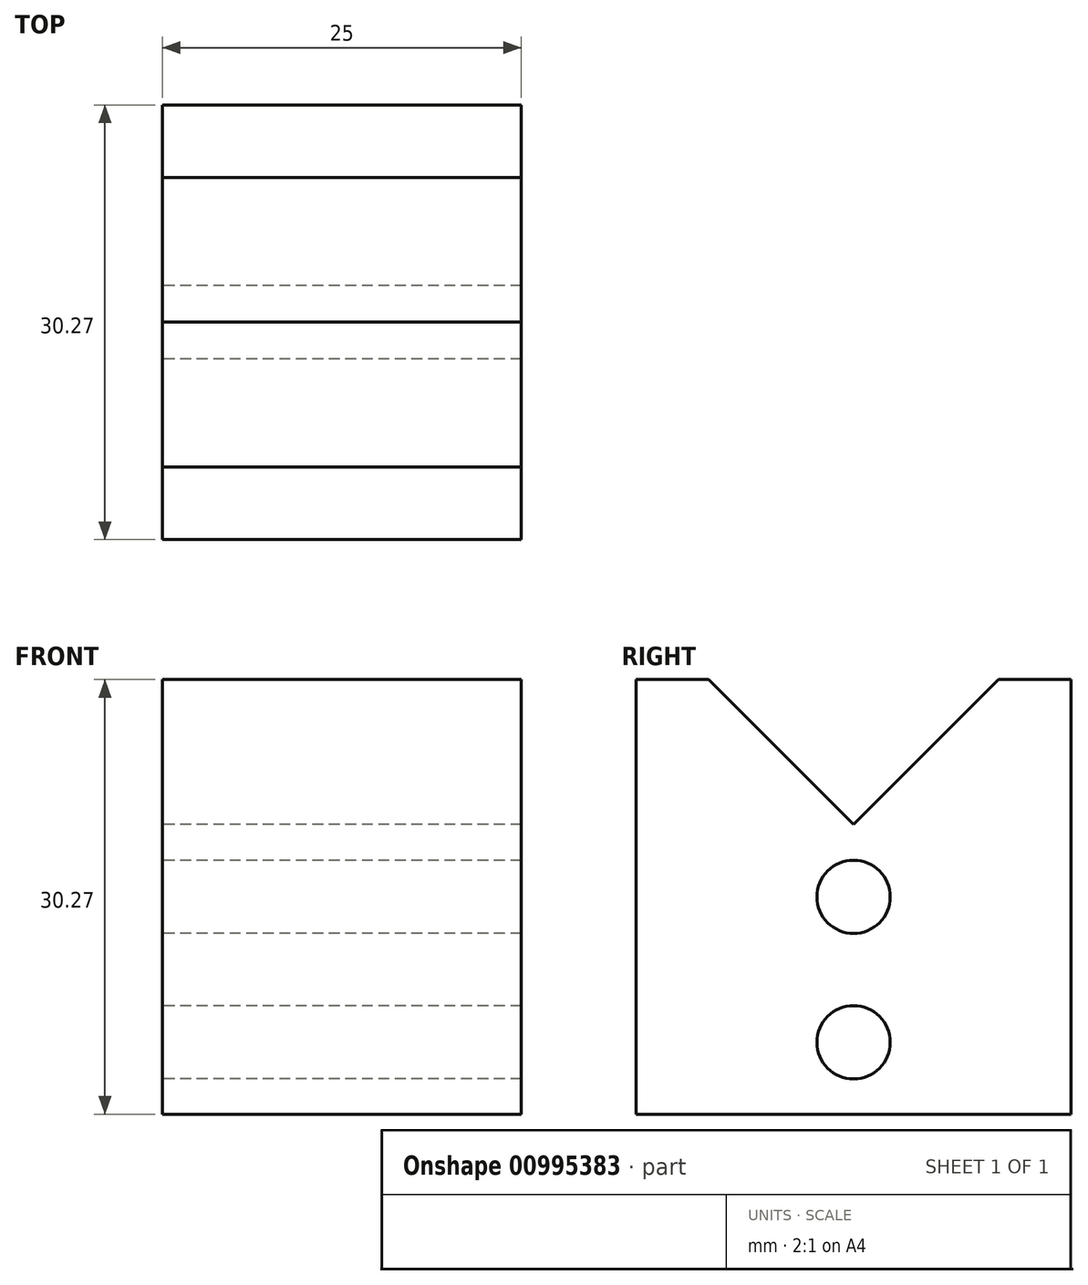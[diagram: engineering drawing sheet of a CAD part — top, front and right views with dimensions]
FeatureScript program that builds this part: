
annotation { "Feature Type Name" : "Feature", "Feature Type Description" : "" }
export const myFeature = defineFeature(function(context is Context, id is Id, definition is map)
    precondition{}
    {
        {
            var Q0;
            Q0=qCreatedBy(makeId("Right.planeOp"),FACE);
            var sketch = newSketch(context, id + "F0", { "sketchPlane" : qUnion([Q0])});
            skLineSegment(sketch, "E0.top", {"start": v(19.07, 30.27) * mm, "end": v(49.34, 30.27) * mm});
            skLineSegment(sketch, "E0.left", {"start": v(19.07, 0) * mm, "end": v(19.07, 30.27) * mm});
            skLineSegment(sketch, "E0.right", {"start": v(49.34, 0) * mm, "end": v(49.34, 30.27) * mm});
            skLineSegment(sketch, "E1", {"start": v(34.2, 20.18) * mm, "end": v(44.3, 30.27) * mm});
            skLineSegment(sketch, "E2", {"start": v(34.2, 20.18) * mm, "end": v(24.12, 30.27) * mm});
            skLineSegment(sketch, "E3", {"start": v(34.2, 30.27) * mm, "end": v(44.3, 30.27) * mm, "construction": true});
            skLineSegment(sketch, "E4", {"start": v(19.07, 0) * mm, "end": v(49.34, 0) * mm});
            skLineSegment(sketch, "E5", {"start": v(34.2, 20.18) * mm, "end": v(34.2, 0) * mm, "construction": true});
            skLineSegment(sketch, "E6", {"start": v(49.34, 30.27) * mm, "end": v(19.07, 0) * mm, "construction": true});
            skLineSegment(sketch, "E7", {"start": v(19.07, 30.27) * mm, "end": v(49.34, 0) * mm, "construction": true});
            skPoint(sketch, "E8", {"position": v(34.2, 15.14) * mm});
            skPoint(sketch, "E9", {"position": v(34.2, 10.1) * mm});
            skPoint(sketch, "E10", {"position": v(34.2, 5) * mm});
            skSolve(sketch);
        }
        {
            var Q0;
            Q0=makeQuery(id+"F0.imprint","IMPRINT",FACE,{"disambiguationData":[TD([[makeQuery(id+"F0.imprint","IMPRINT",EDGE,{"derivedFrom":sQuery(id+"F0.wireOp",EDGE,"E0.bottom")}),1.0]])]});
            var Q1;
            {var subQ1=sQuery(id+"F0.wireOp",EDGE,"E0.left");Q1=makeQuery(id+"F0.imprint","IMPRINT",FACE,{"disambiguationData":[TD([[makeQuery(id+"F0.imprint","IMPRINT",EDGE,{"derivedFrom":subQ1}),-1.0]])]});}
            extrude(context, id + "F1", {"entities" : qUnion([Q0, Q1]), "depth" : 25 * mm, "offsetDistance" : 25 * mm});
        }
        {
            var Q0;
            Q0=sQuery(id+"F0.wireOp",VERTEX,"E10");
            var Q1;
            Q1=sQuery(id+"F0.wireOp",VERTEX,"E8");
            var Q2;
            Q2=makeQuery(id+"F1.opExtrude","SWEPT_BODY",BODY,{"disambiguationData":[OSD([sQuery(id+"F0.wireOp",EDGE,"E0.top"),sQuery(id+"F0.wireOp",EDGE,"E0.left"),sQuery(id+"F0.wireOp",EDGE,"E0.right"),sQuery(id+"F0.wireOp",EDGE,"E1"),sQuery(id+"F0.wireOp",EDGE,"E2"),sQuery(id+"F0.wireOp",EDGE,"E4")])]});
            hole(context, id + "F2", {"style" : HoleStyle.SIMPLE, "endStyle" : HoleEndStyle.THROUGH, "oppositeDirection" : true, "holeDiameter" : 5.1 * mm, "majorDiameter" : 5 * mm, "isTappedThrough" : true, "tappedDepth" : 12 * mm, "tapClearance" : 3, "locations" : qUnion([Q0, Q1]), "scope" : qUnion([Q2])});
        }
    });
